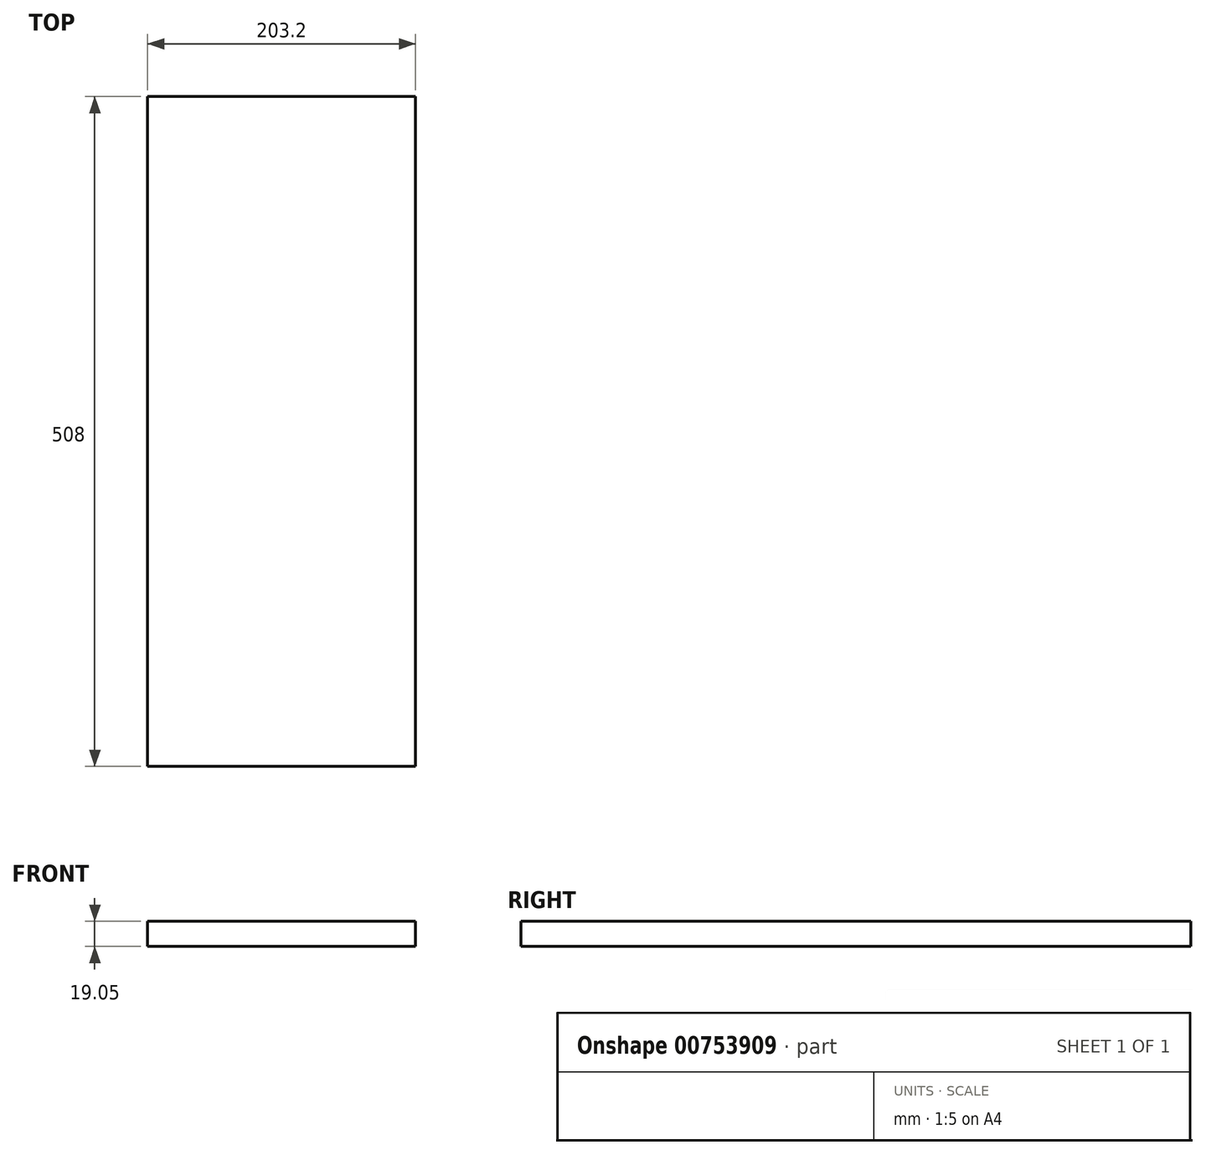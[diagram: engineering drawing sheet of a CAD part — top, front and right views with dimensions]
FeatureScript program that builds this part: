
annotation { "Feature Type Name" : "Feature", "Feature Type Description" : "" }
export const myFeature = defineFeature(function(context is Context, id is Id, definition is map)
    precondition{}
    {
        {
            var Q0;
            Q0=qCreatedBy(makeId("Top.planeOp"),FACE);
            var sketch = newSketch(context, id + "F0", { "sketchPlane" : qUnion([Q0])});
            skLineSegment(sketch, "E0.bottom", {"start": v(101.6, -254) * mm, "end": v(-101.6, -254) * mm});
            skLineSegment(sketch, "E0.top", {"start": v(101.6, 254) * mm, "end": v(-101.6, 254) * mm});
            skLineSegment(sketch, "E0.left", {"start": v(101.6, -254) * mm, "end": v(101.6, 254) * mm});
            skLineSegment(sketch, "E0.right", {"start": v(-101.6, -254) * mm, "end": v(-101.6, 254) * mm});
            skPoint(sketch, "E0.middle", {"position": v(0, 0) * mm});
            skSolve(sketch);
        }
        {
            var Q0;
            Q0=makeQuery(id+"F0.imprint","IMPRINT",FACE,{"disambiguationData":[TD([[makeQuery(id+"F0.imprint","IMPRINT",EDGE,{"derivedFrom":sQuery(id+"F0.wireOp",EDGE,"E0.bottom")}),-1.0]])]});
            extrude(context, id + "F1", {"entities" : qUnion([Q0]), "depth" : 19.05 * mm, "offsetDistance" : 25.4 * mm});
        }
    });
